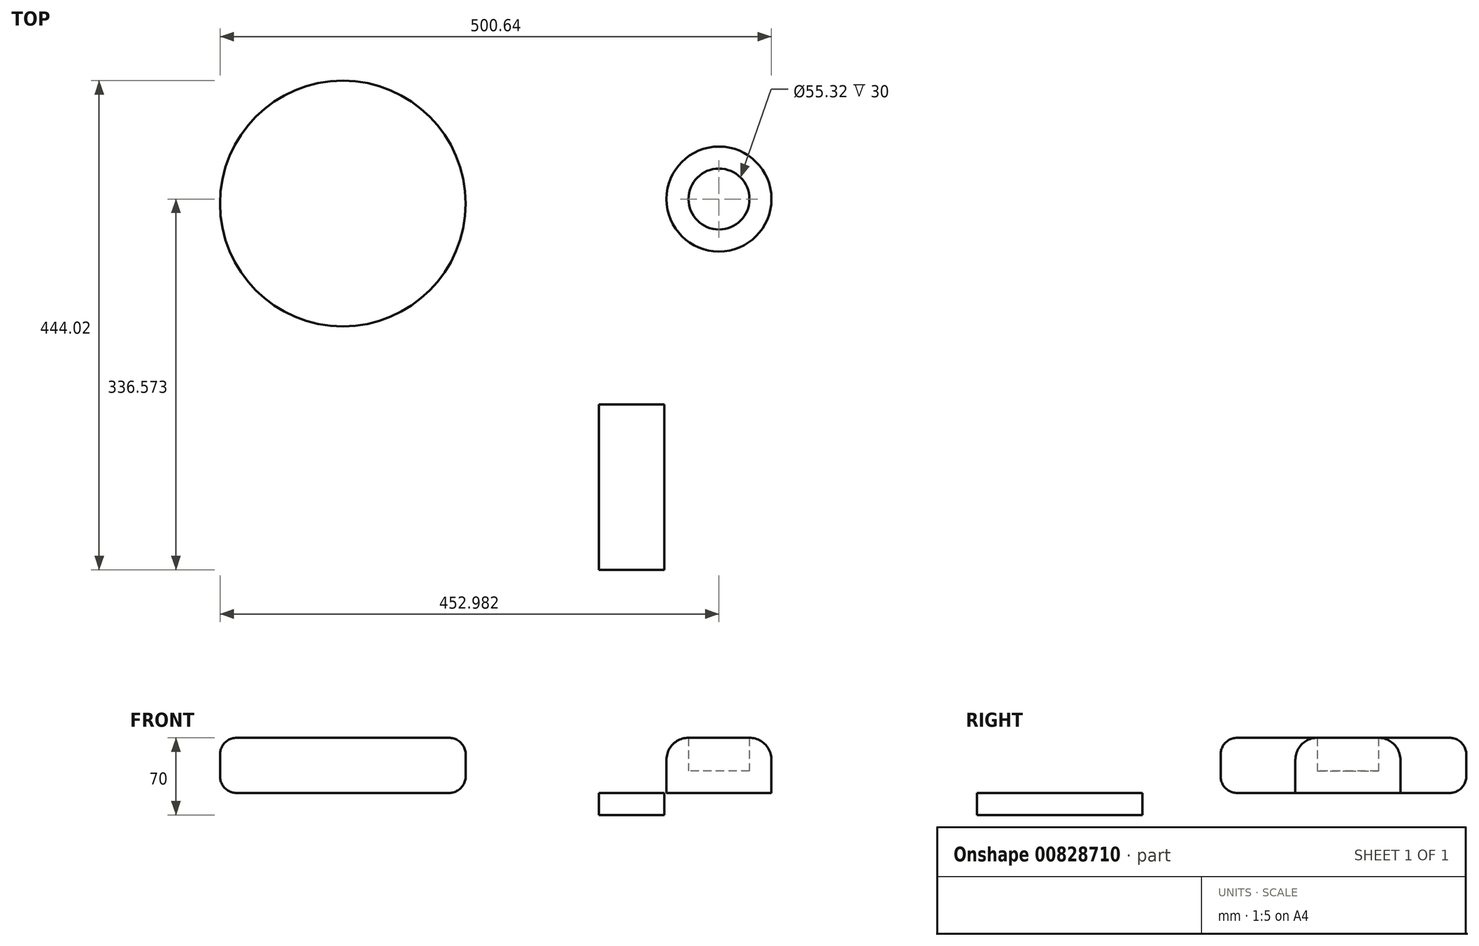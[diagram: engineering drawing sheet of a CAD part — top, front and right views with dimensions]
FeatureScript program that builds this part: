
annotation { "Feature Type Name" : "Feature", "Feature Type Description" : "" }
export const myFeature = defineFeature(function(context is Context, id is Id, definition is map)
    precondition{}
    {
        {
            var Q0;
            Q0=qCreatedBy(makeId("Top.planeOp"),FACE);
            var sketch = newSketch(context, id + "F0", { "sketchPlane" : qUnion([Q0])});
            skLineSegment(sketch, "E0.bottom", {"start": v(-113.54, -249.62) * mm, "end": v(-172.89, -249.62) * mm});
            skLineSegment(sketch, "E0.top", {"start": v(-113.54, -399.62) * mm, "end": v(-172.89, -399.62) * mm});
            skLineSegment(sketch, "E0.left", {"start": v(-113.54, -249.62) * mm, "end": v(-113.54, -399.62) * mm});
            skLineSegment(sketch, "E0.right", {"start": v(-172.89, -249.62) * mm, "end": v(-172.89, -399.62) * mm});
            skPoint(sketch, "E0.middle", {"position": v(-143.22, -324.62) * mm});
            skSolve(sketch);
        }
        {
            var Q0;
            Q0 = qSketchRegion(id + "F0", true);
            extrude(context, id + "F1", {"entities" : qUnion([Q0]), "oppositeDirection" : true, "depth" : 20 * mm, "offsetDistance" : 25 * mm});
        }
        {
            var Q0;
            Q0=qCreatedBy(makeId("Top.planeOp"),FACE);
            var sketch = newSketch(context, id + "F2", { "sketchPlane" : qUnion([Q0])});
            skCircle(sketch, "E1", {"center": v(-63.78, -63.05) * mm, "radius": 47.66 * mm});
            skSolve(sketch);
        }
        {
            var Q0;
            Q0=makeQuery(id+"F2.imprint","IMPRINT",FACE,{"disambiguationData":[TD([[makeQuery(id+"F2.imprint","IMPRINT",EDGE,{"derivedFrom":sQuery(id+"F2.wireOp",EDGE,"E1")}),1.0]])]});
            extrude(context, id + "F3", {"entities" : qUnion([Q0]), "operationType" : NewBodyOperationType.ADD, "depth" : 50 * mm, "offsetDistance" : 25 * mm});
        }
        {
            var Q0;
            Q0=makeQuery(id+"F3.opExtrude","CAP_EDGE",EDGE,{"disambiguationData":[OSD([sQuery(id+"F2.wireOp",EDGE,"E1")])],"isStart":false});
            fillet(context, id + "F4", {"entities" : qUnion([Q0]), "radius" : 20 * mm, "tangentPropagation" : true, "allowEdgeOverflow" : false});
        }
        {
            var Q0;
            Q0=makeQuery(id+"F3.opExtrude","CAP_FACE",FACE,{"disambiguationData":[OSD([sQuery(id+"F2.wireOp",EDGE,"E1")])],"isStart":false});
            shell(context, id + "F5", {"entities" : qUnion([Q0]), "thickness" : 20 * mm});
        }
        {
            var Q0;
            Q0=qCreatedBy(makeId("Top.planeOp"),FACE);
            var sketch = newSketch(context, id + "F6", { "sketchPlane" : qUnion([Q0])});
            skCircle(sketch, "E2", {"center": v(-405.26, -67.1) * mm, "radius": 111.5 * mm});
            skSolve(sketch);
        }
        {
            var Q0;
            Q0=makeQuery(id+"F6.imprint","IMPRINT",FACE,{"disambiguationData":[TD([[makeQuery(id+"F6.imprint","IMPRINT",EDGE,{"derivedFrom":sQuery(id+"F6.wireOp",EDGE,"E2")}),1.0]])]});
            extrude(context, id + "F7", {"entities" : qUnion([Q0]), "depth" : 50 * mm, "offsetDistance" : 25 * mm});
        }
        {
            var Q0;
            Q0=makeQuery(id+"F7.opExtrude","CAP_EDGE",EDGE,{"disambiguationData":[OSD([sQuery(id+"F6.wireOp",EDGE,"E2")])],"isStart":false});
            fillet(context, id + "F8", {"entities" : qUnion([Q0]), "radius" : 15 * mm, "tangentPropagation" : true, "allowEdgeOverflow" : false});
        }
        {
            var Q0;
            Q0=makeQuery(id+"F7.opExtrude","CAP_EDGE",EDGE,{"disambiguationData":[OSD([sQuery(id+"F6.wireOp",EDGE,"E2")])],"isStart":true});
            fillet(context, id + "F9", {"entities" : qUnion([Q0]), "radius" : 15 * mm, "tangentPropagation" : true, "allowEdgeOverflow" : false});
        }
    });
